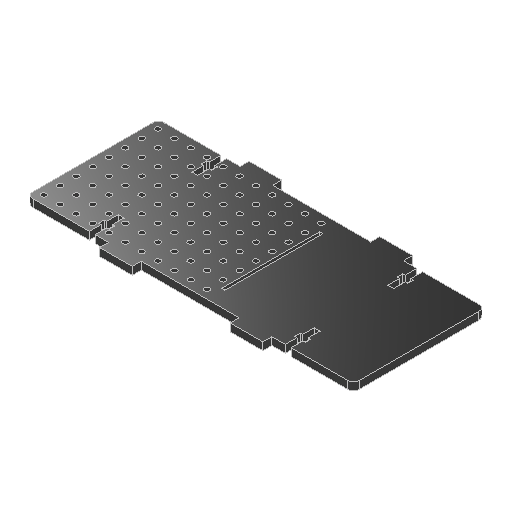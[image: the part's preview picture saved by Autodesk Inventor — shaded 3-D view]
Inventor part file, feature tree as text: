
AUTODESK INVENTOR PART (.ipt)
format: ipt  version: 2025 (Build 290162000, 162)  size: 322,048 bytes
history: native  units: mm
features: sketch x6, extrude x4, mirror x2, hole x2, plane x1, fillet x1, pattern_linear x1, projected_geometry x1
ambient origin geometry x8: Origin, YZ Plane, XZ Plane, XY Plane, X Axis, Y Axis, Z Axis, Center Point
bodies: Solid1 (feature_tree)
feature tree (18):
  extrude  "Extrusion1"  Depth=6.0mm
  plane  "Work Plane1"
  extrude  "Extrusion2"  Depth=6.0mm
  mirror  "Mirror1"
  extrude  "Extrusion3"  Depth=102.3mm
  fillet  "Fillet1"  Radius=7.0mm
  mirror  "Mirror2"
  hole  "Hole1"  [1 undecoded]
  pattern_linear  "Rectangular Pattern1"  Spacing1=254.0mm  [1 undecoded]
  extrude  "Extrusion5"  Depth=6.0mm
  hole  "Hole2"  [1 undecoded]
  sketch  "Sketch1"  dims[d1=6.0mm d2=0.0mm d3=6.7mm]
  sketch  "Sketch2"  dims[d4=4.25mm d5=6.0mm d6=4.0mm d7=2.0mm d8=90.0deg d9=8.0mm d10=20.594885mm d11=110.0mm d13=12.7mm d14=80.0mm d16=12.7mm]
  sketch  "Sketch3"  dims[d17=5.0mm d19=102.3mm d20=7.0mm]
  projected_geometry  "Projected Loop1"
  sketch  "Sketch4"  dims[d21=76.2mm d22=0.0mm d23=0.0mm]
  sketch  "Sketch6"  dims[d24=22.5mm d25=4.25mm d26=8.25mm d28=4.4958mm]
  sketch  "Sketch7"  dims[d29=0.0mm d30=0.0mm d31=254.0mm d32=25.4mm d43=76.2mm d44=76.2mm d45=6.35mm d50=2.54mm d51=76.2mm d53=139.7mm d56=2.54mm d57=0.0mm d58=4.5mm d59=6.0mm d60=4.0mm d61=2.0mm d62=90.0deg d63=8.0mm d64=0.0mm]
note: 3 required parameter values undecoded (feature->parameter linkage not recoverable at this tier; creation-order binding heuristic only, values carry confidence <= 0.55)
